# Revit family: CVS-Axial Jetfan
name_source: partatom
category: Mechanical Equipment
revit_build: Autodesk Revit 2018 (Build: 20170223_1515(x64)
units: mm (PartAtom-declared; Revit-internal decimal feet)

## family parameters
Always vertical = Yes
Cut with Voids When Loaded = No
OmniClass Number = 23.75.00.00
OmniClass Title = Climate Control (HVAC)
Part Type = Normal
Room Calculation Point = Yes
Round Connector Dimension = Use Diameter
Shared = No
Work Plane-Based = No

## types (2) — shared parameters
Blade Visible = Yes
Casing Material = Galvanised Sheet With Electrostatic Paint
Clarification = Axial Jet Fan, double speed motor for daily ventilation and in case of fire, F300, F400 fire resistance. maximum thrust and low sound level with existing aerofoil blade, high resistance of corrosion due to electrostatic oven painted case, wire guard in sunction side, deflector in discharge side ( double deflector in reversible models)
Damper2 Length = 395 mm  [stored 1.29593 ft]
Description = AXIAL JET FAN
Fan Diameter = 400 mm  [stored 1.31234 ft]
Fan Length = 1850 mm  [stored 6.06955 ft]
Fan Radius = 250 mm  [stored 0.82021 ft]
Fan Void = 480 mm  [stored 1.5748 ft]
Fan Void Half = 240 mm  [stored 0.787402 ft]
Frequency = 50 Hz
Impeller Material = Aluminum
Insulation Class = H
Jet Fan Diameter = 500 mm  [stored 1.64042 ft]
Load Classification = Mechanical
ML = 348 mm  [stored 1.14173 ft]
MR = 200 mm  [stored 0.656168 ft]
Manufacturer = Cvsair
Max. Motor Power = 2000 W
Min. Motor Power = 500 W
Modeled By = SAINA ENG.
Motor Protection Class = IP 55
Nested Middle Fan Void = 450 mm  [stored 1.47638 ft]
Nominal Speed(rpm) = 1415 / 2835
Operating Temperature(°C) = F300; F400
F300; F400
F300; F400
Phase(Ph) = 3
Power Factor = 1
Product Certificates = CE; EN 12101-3
Product Description = Double speed motor, galvanised sheet with electrostatic paint, Sound-attenuator fan casing, wire guard and deflector, F300 and F400 fire rated Axial Jet Fan
Production Place = Turkey
Support Height = 260 mm  [stored 0.853018 ft]
Support Material = Galvanised Sheet
Support Width = 450 mm  [stored 1.47638 ft]
URL = https://cvsair.com.tr
Voltage = 400 V
Web = https://cvsair.com.tr

## per-type parameters (varying)
| type | Max. Air Flow | Min. Air Flow | Thrust(N) |
| AJ-TR-400 | 9260 m³/h | 4630 m³/h | 16 / 62 |
| AJ400-80 | 10440 m³/h | 5220 m³/h | 20/80 |

note: column(s) folded — value = type name in every type: Model

note: [stored X ft] marks values corroborated as IEEE doubles in the binary element streams (Revit-internal decimal feet)

## geometry (parser evidence)
native form markers: Blend x2, Extrusion x4, Sweep x4
no freeform markers — native parametric forms only
